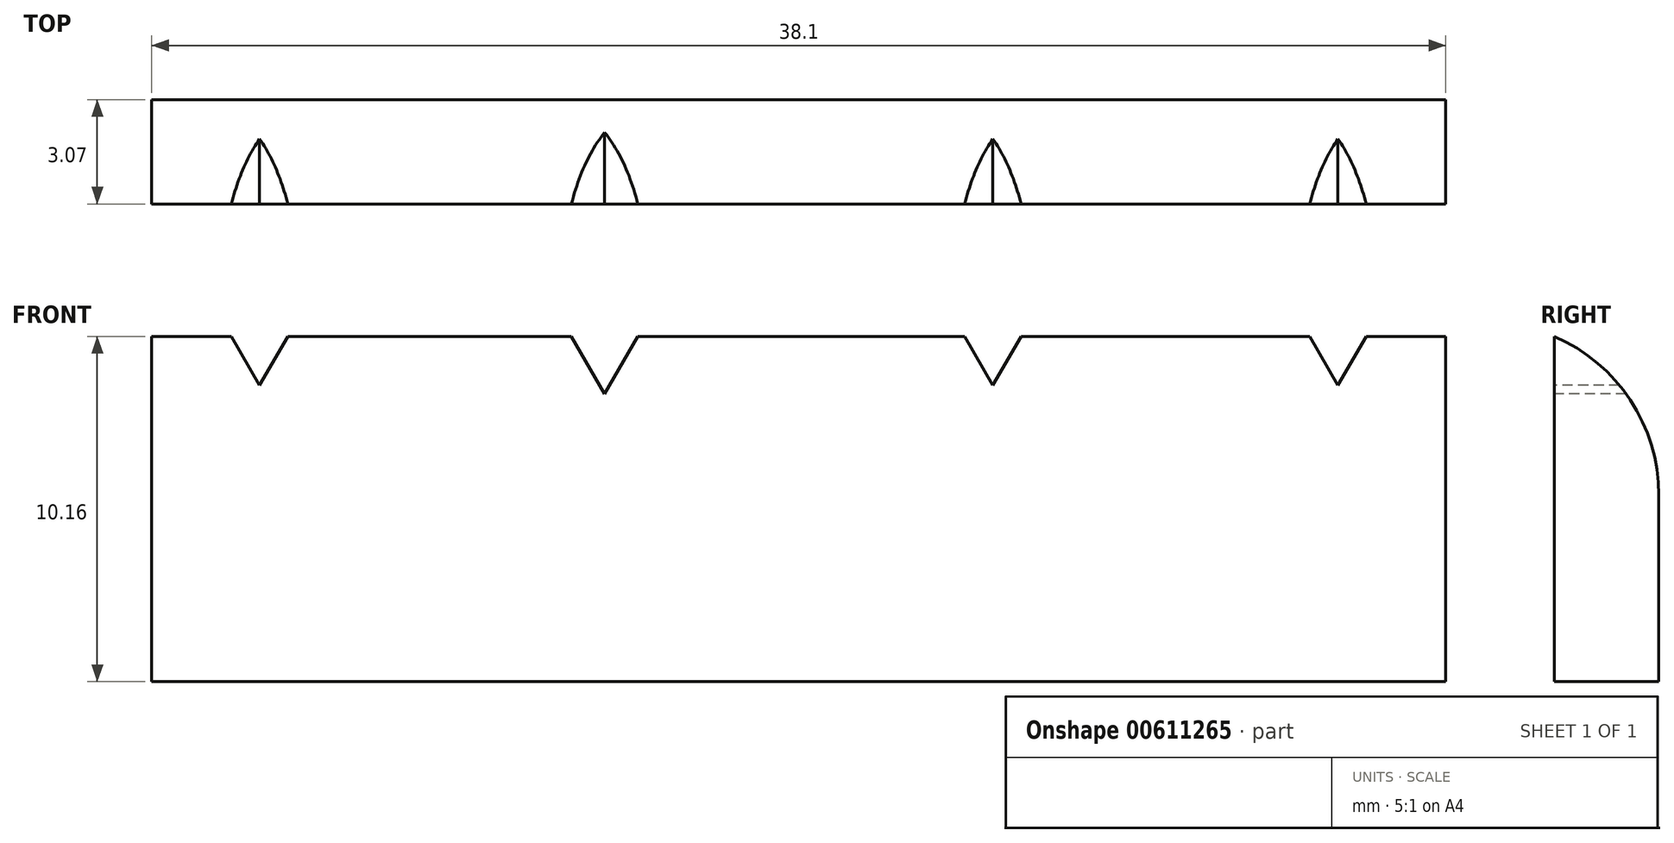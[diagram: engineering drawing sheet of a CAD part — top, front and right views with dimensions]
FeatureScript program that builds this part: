
annotation { "Feature Type Name" : "Feature", "Feature Type Description" : "" }
export const myFeature = defineFeature(function(context is Context, id is Id, definition is map)
    precondition{}
    {
        {
            var Q0;
            Q0=qCreatedBy(makeId("Top.planeOp"),FACE);
            var sketch = newSketch(context, id + "F0", { "sketchPlane" : qUnion([Q0])});
            skLineSegment(sketch, "E0.bottom", {"start": v(-19.05, 0) * mm, "end": v(19.05, 0) * mm});
            skLineSegment(sketch, "E0.top", {"start": v(-19.05, 3.07) * mm, "end": v(19.05, 3.07) * mm});
            skLineSegment(sketch, "E0.left", {"start": v(-19.05, 0) * mm, "end": v(-19.05, 3.07) * mm});
            skLineSegment(sketch, "E0.right", {"start": v(19.05, 0) * mm, "end": v(19.05, 3.07) * mm});
            skSolve(sketch);
        }
        {
            var Q0;
            Q0=makeQuery(id+"F0.imprint","IMPRINT",FACE,{"disambiguationData":[TD([[makeQuery(id+"F0.imprint","IMPRINT",EDGE,{"derivedFrom":sQuery(id+"F0.wireOp",EDGE,"E0.bottom")}),1.0]])]});
            extrude(context, id + "F1", {"entities" : qUnion([Q0]), "depth" : 10.16 * mm, "offsetDistance" : 25.4 * mm});
        }
        {
            var Q0;
            Q0=makeQuery(id+"F1.opExtrude","SWEPT_FACE",FACE,{"disambiguationData":[OSD([sQuery(id+"F0.wireOp",EDGE,"E0.bottom")])]});
            var sketch = newSketch(context, id + "F2", { "sketchPlane" : qUnion([Q0])});
            skCircle(sketch, "E1.cCircle", {"center": v(-15.88, 10.19) * mm, "radius": 0.73 * mm, "construction": true});
            skLineSegment(sketch, "E1.0", {"start": v(-14.6, 10.92) * mm, "end": v(-15.88, 8.72) * mm});
            skLineSegment(sketch, "E1.1", {"start": v(-15.88, 8.72) * mm, "end": v(-17.14, 10.92) * mm});
            skLineSegment(sketch, "E1.2", {"start": v(-17.14, 10.92) * mm, "end": v(-14.6, 10.92) * mm});
            skPoint(sketch, "E1.0.midPoint", {"position": v(-15.24, 9.82) * mm});
            skCircle(sketch, "E2.cCircle", {"center": v(-5.72, 9.93) * mm, "radius": 0.73 * mm, "construction": true});
            skLineSegment(sketch, "E2.0", {"start": v(-4.45, 10.67) * mm, "end": v(-5.71, 8.47) * mm});
            skLineSegment(sketch, "E2.1", {"start": v(-5.72, 8.47) * mm, "end": v(-6.99, 10.67) * mm});
            skLineSegment(sketch, "E2.2", {"start": v(-6.98, 10.67) * mm, "end": v(-4.45, 10.67) * mm});
            skPoint(sketch, "E2.0.midPoint", {"position": v(-5.08, 9.57) * mm});
            skCircle(sketch, "E3.cCircle", {"center": v(15.87, 10.19) * mm, "radius": 0.73 * mm, "construction": true});
            skLineSegment(sketch, "E3.0", {"start": v(17.14, 10.92) * mm, "end": v(15.87, 8.72) * mm});
            skLineSegment(sketch, "E3.1", {"start": v(15.88, 8.72) * mm, "end": v(14.6, 10.92) * mm});
            skLineSegment(sketch, "E3.2", {"start": v(14.6, 10.92) * mm, "end": v(17.14, 10.92) * mm});
            skPoint(sketch, "E3.0.midPoint", {"position": v(16.5, 9.82) * mm});
            skCircle(sketch, "E4.cCircle", {"center": v(5.72, 10.19) * mm, "radius": 0.73 * mm, "construction": true});
            skLineSegment(sketch, "E4.0", {"start": v(6.99, 10.92) * mm, "end": v(5.72, 8.72) * mm});
            skLineSegment(sketch, "E4.1", {"start": v(5.72, 8.72) * mm, "end": v(4.45, 10.92) * mm});
            skLineSegment(sketch, "E4.2", {"start": v(4.44, 10.92) * mm, "end": v(6.98, 10.92) * mm});
            skPoint(sketch, "E4.0.midPoint", {"position": v(6.35, 9.82) * mm});
            skSolve(sketch);
        }
        {
            var Q0;
            Q0=makeQuery(id+"F1.opExtrude","CAP_EDGE",EDGE,{"disambiguationData":[OSD([sQuery(id+"F0.wireOp",EDGE,"E0.top")])],"isStart":false});
            fillet(context, id + "F3", {"entities" : qUnion([Q0]), "radius" : 5.08 * mm, "tangentPropagation" : true, "allowEdgeOverflow" : false});
        }
        {
            var Q0;
            {var subQ0=sQuery(id+"F2.wireOp",EDGE,"E1.1");var subQ1=sQuery(id+"F2.wireOp",EDGE,"E1.0");var subQ2=makeQuery(id+"F2.imprint","INTERSECT",VERTEX,{"derivedFrom":[subQ1,subQ0]});Q0=makeQuery(id+"F2.imprint","IMPRINT",FACE,{"disambiguationData":[TD([[makeQuery(id+"F2.imprint","IMPRINT",EDGE,{"disambiguationData":[TD([[subQ2,1.0]])],"derivedFrom":subQ1}),-1.0]])]});}
            var Q1;
            {var subQ0=sQuery(id+"F2.wireOp",EDGE,"E2.1");var subQ1=sQuery(id+"F2.wireOp",EDGE,"E2.0");var subQ2=makeQuery(id+"F2.imprint","INTERSECT",VERTEX,{"derivedFrom":[subQ1,subQ0]});Q1=makeQuery(id+"F2.imprint","IMPRINT",FACE,{"disambiguationData":[TD([[makeQuery(id+"F2.imprint","IMPRINT",EDGE,{"disambiguationData":[TD([[subQ2,1.0]])],"derivedFrom":subQ1}),-1.0]])]});}
            var Q2;
            {var subQ0=sQuery(id+"F2.wireOp",EDGE,"E4.1");var subQ1=sQuery(id+"F2.wireOp",EDGE,"E4.0");var subQ2=makeQuery(id+"F2.imprint","INTERSECT",VERTEX,{"derivedFrom":[subQ1,subQ0]});Q2=makeQuery(id+"F2.imprint","IMPRINT",FACE,{"disambiguationData":[TD([[makeQuery(id+"F2.imprint","IMPRINT",EDGE,{"disambiguationData":[TD([[subQ2,1.0]])],"derivedFrom":subQ1}),-1.0]])]});}
            var Q3;
            {var subQ0=sQuery(id+"F2.wireOp",EDGE,"E3.1");var subQ1=sQuery(id+"F2.wireOp",EDGE,"E3.0");var subQ2=makeQuery(id+"F2.imprint","INTERSECT",VERTEX,{"derivedFrom":[subQ1,subQ0]});Q3=makeQuery(id+"F2.imprint","IMPRINT",FACE,{"disambiguationData":[TD([[makeQuery(id+"F2.imprint","IMPRINT",EDGE,{"disambiguationData":[TD([[subQ2,1.0]])],"derivedFrom":subQ1}),-1.0]])]});}
            extrude(context, id + "F4", {"entities" : qUnion([Q0, Q1, Q2, Q3]), "operationType" : NewBodyOperationType.REMOVE, "oppositeDirection" : true, "depth" : 25.4 * mm, "offsetDistance" : 25.4 * mm});
        }
    });
